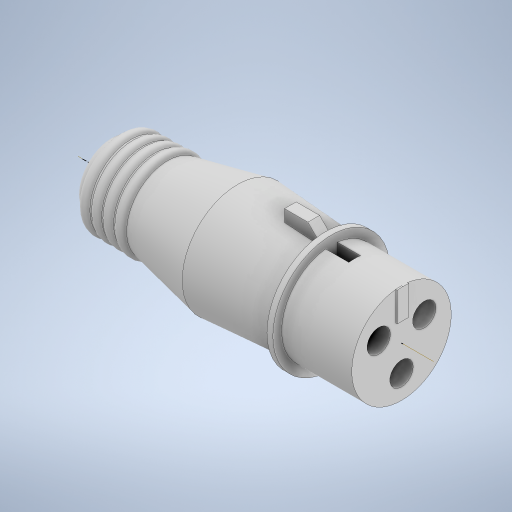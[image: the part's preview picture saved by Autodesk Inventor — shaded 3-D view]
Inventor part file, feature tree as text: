
AUTODESK INVENTOR PART (.ipt)
format: ipt  version: 2023 (Build 270158000, 158)  size: 429,056 bytes
history: native  units: in
note: dims shown in document units (in); Inventor stores cm internally (conversion verified against a paired STEP export)
features: sketch x12, plane x8, extrude x7, other x3, revolve x2, hole x1, projected_geometry x1
ambient origin geometry x8: Origin, YZ Plane, XZ Plane, XY Plane, X Axis, Y Axis, Z Axis, Center Point
bodies: Solid1 (feature_tree)
feature tree (34):
  revolve  "Revolution1"  [1 undecoded]
  plane  "Work Plane1"
  extrude  "Extrusion1"  Depth=0.0591in
  plane  "Work Plane2"
  hole  "Hole1"  [1 undecoded]
  plane  "Work Plane3"
  extrude  "Extrusion2"  Depth=0.4724in
  extrude  "Extrusion3"  Depth=0.2756in
  extrude  "Extrusion4"  Depth=0.0591in
  plane  "Work Plane4"
  extrude  "Extrusion5"  TaperAngle=0.0deg  [1 undecoded]
  plane  "Work Plane6"
  extrude  "Extrusion6"  Depth=0.1969in
  extrude  "Extrusion7"  Depth=0.0098in TaperAngle=0.0deg
  sketch  "Sketch10"  dims[d20=0.0in]
  sketch  "Sketch11"  dims[d21=0.1575in d22=0.2362in d23=0.1575in d24=0.0787in d25=90.0deg d26=0.1575in d27=0.0in d28=0.2362in]
  other  "Work Axis1"
  other  "Work Axis2"
  other  "Work Axis3"
  plane  "Work Plane8"
  sketch  "Sketch12"  dims[d29=0.0394in d30=0.0394in d31=0.0787in d32=0.1575in d33=0.0in d34=0.0787in d35=0.1575in d36=0.0in d37=0.0394in d38=0.0in d39=0.1575in d40=0.0787in d41=0.0in d42=-0.0787in d43=0.0197in d44=0.0394in d45=0.0in d46=0.0197in d47=0.0394in d48=0.0in d49=-0.2756in d50=360.0deg d15=0.0394in d51=0.0344in]
  revolve  "Revolution2"  [1 undecoded]
  sketch  "Sketch1"  dims[d0=1.9685in d1=0.3346in]
  sketch  "Sketch2"  dims[d2=0.4724in d3=0.0591in]
  sketch  "Sketch3"  dims[d4=0.0394in d5=1.8898in]
  sketch  "Sketch4"  dims[d6=0.315in d7=0.4724in]
  sketch  "Sketch5"  dims[d8=0.374in d9=0.2756in]
  sketch  "Sketch6"  dims[d10=0.2362in d11=0.0591in]
  sketch  "Sketch7"  dims[d12=90.0deg d13=0.0in]
  plane  "Work Plane5"
  sketch  "Sketch8"  dims[d14=0.1969in d16=0.1969in]
  projected_geometry  "Projected Loop1"
  sketch  "Sketch9"  dims[d17=0.0787in d18=0.0098in d19=0.0in]
  plane  "Work Plane7"
note: 4 required parameter values undecoded (feature->parameter linkage not recoverable at this tier; creation-order binding heuristic only, values carry confidence <= 0.55)